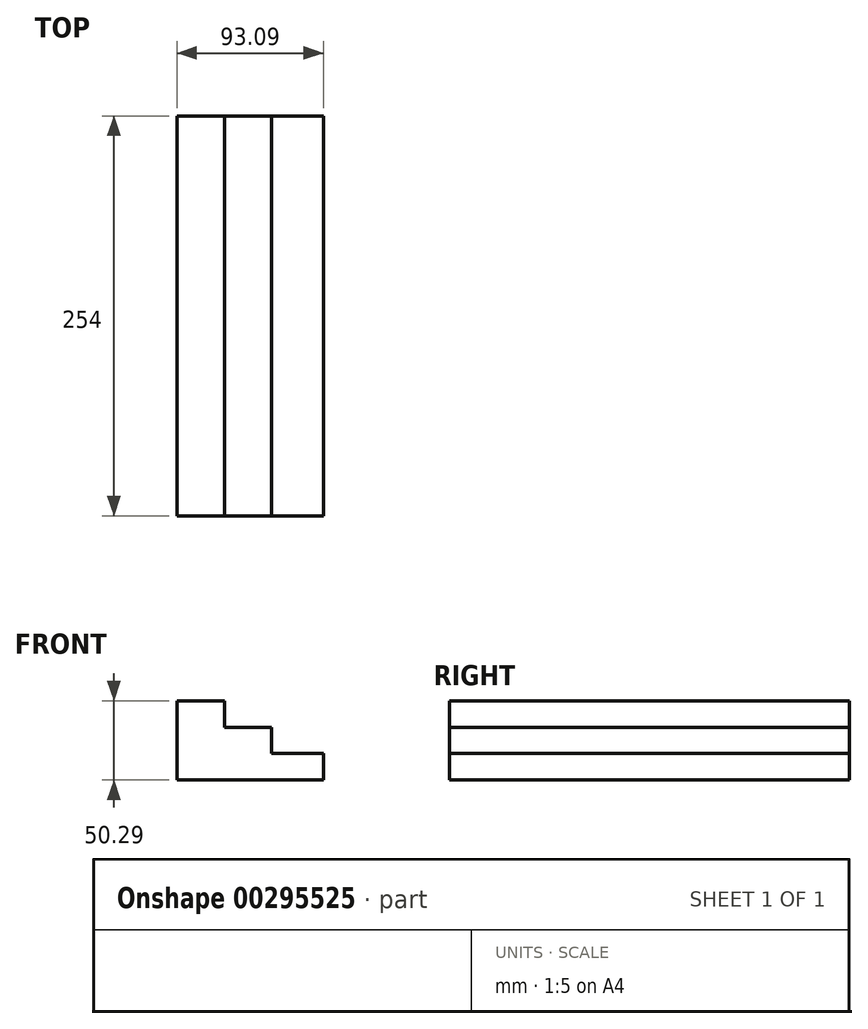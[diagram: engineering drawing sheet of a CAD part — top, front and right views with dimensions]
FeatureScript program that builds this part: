
annotation { "Feature Type Name" : "Feature", "Feature Type Description" : "" }
export const myFeature = defineFeature(function(context is Context, id is Id, definition is map)
    precondition{}
    {
        {
            var Q0;
            Q0=qCreatedBy(makeId("Front.planeOp"),FACE);
            var sketch = newSketch(context, id + "F0", { "sketchPlane" : qUnion([Q0])});
            skLineSegment(sketch, "E0.bottom", {"start": v(0, 0) * mm, "end": v(30.4, 0) * mm});
            skLineSegment(sketch, "E0.top", {"start": v(0, -16.76) * mm, "end": v(30.4, -16.76) * mm});
            skLineSegment(sketch, "E0.left", {"start": v(0, 0) * mm, "end": v(0, -16.76) * mm});
            skLineSegment(sketch, "E0.right", {"start": v(30.4, 0) * mm, "end": v(30.4, -16.76) * mm});
            skLineSegment(sketch, "E1.bottom", {"start": v(0, -16.76) * mm, "end": v(60.1, -16.76) * mm});
            skLineSegment(sketch, "E1.top", {"start": v(0, -33.53) * mm, "end": v(60.1, -33.53) * mm});
            skLineSegment(sketch, "E1.left", {"start": v(0, -16.76) * mm, "end": v(0, -33.53) * mm});
            skLineSegment(sketch, "E1.right", {"start": v(60.1, -16.76) * mm, "end": v(60.1, -33.53) * mm});
            skLineSegment(sketch, "E2.bottom", {"start": v(0, -33.53) * mm, "end": v(93.09, -33.53) * mm});
            skLineSegment(sketch, "E2.top", {"start": v(0, -50.3) * mm, "end": v(93.09, -50.3) * mm});
            skLineSegment(sketch, "E2.left", {"start": v(0, -33.53) * mm, "end": v(0, -50.3) * mm});
            skLineSegment(sketch, "E2.right", {"start": v(93.09, -33.53) * mm, "end": v(93.09, -50.3) * mm});
            skSolve(sketch);
        }
        {
            var Q0;
            Q0 = qSketchRegion(id + "F0", true);
            extrude(context, id + "F1", {"entities" : qUnion([Q0]), "depth" : 254 * mm});
        }
    });
